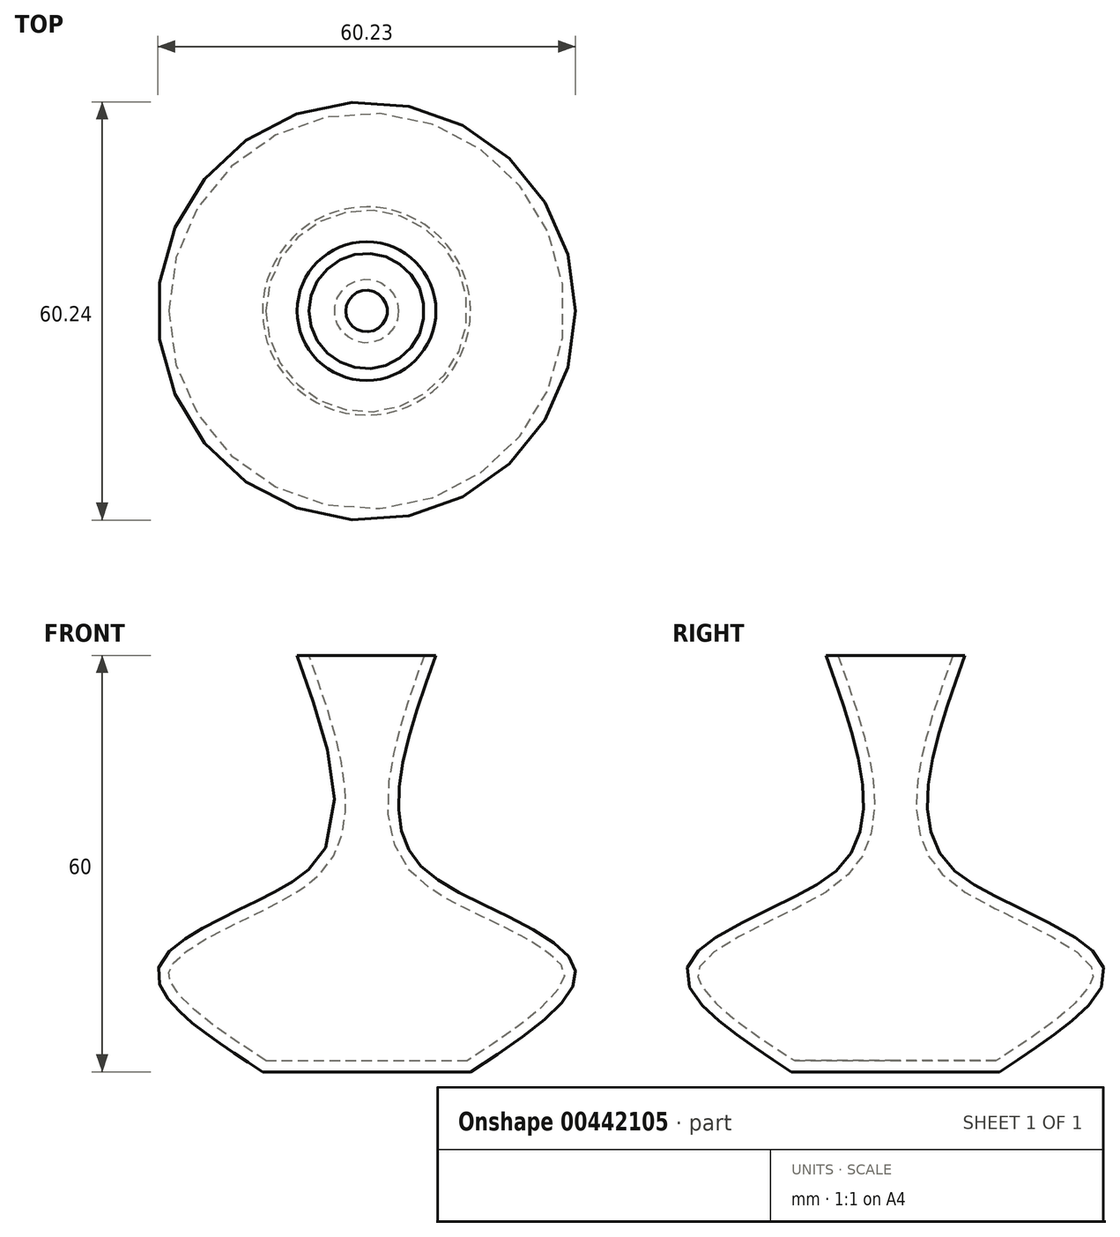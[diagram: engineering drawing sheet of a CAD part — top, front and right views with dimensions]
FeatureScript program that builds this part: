
annotation { "Feature Type Name" : "Feature", "Feature Type Description" : "" }
export const myFeature = defineFeature(function(context is Context, id is Id, definition is map)
    precondition{}
    {
        {
            var Q0;
            Q0=qCreatedBy(makeId("Top.planeOp"),FACE);
            var sketch = newSketch(context, id + "F0", { "sketchPlane" : qUnion([Q0])});
            skCircle(sketch, "E0", {"center": v(0, 0) * mm, "radius": 15 * mm});
            skSolve(sketch);
        }
        {
            var Q0;
            Q0=qCreatedBy(makeId("Top.planeOp"),FACE);
            cPlane(context, id + "F1", {"entities" : qUnion([Q0]), "cplaneType" : CPlaneType.OFFSET, "offset" : 15 * mm, "width" : 150 * mm, "height" : 150 * mm});
        }
        {
            var Q0;
            Q0=qCreatedBy(id+"F1.planeOp",FACE);
            var sketch = newSketch(context, id + "F2", { "sketchPlane" : qUnion([Q0])});
            skCircle(sketch, "E1", {"center": v(0, 0) * mm, "radius": 30 * mm});
            skSolve(sketch);
        }
        {
            var Q0;
            Q0=qCreatedBy(id+"F1.planeOp",FACE);
            cPlane(context, id + "F3", {"entities" : qUnion([Q0]), "cplaneType" : CPlaneType.OFFSET, "offset" : 10 * mm, "width" : 150 * mm, "height" : 150 * mm});
        }
        {
            var Q0;
            Q0=qCreatedBy(id+"F3.planeOp",FACE);
            var sketch = newSketch(context, id + "F4", { "sketchPlane" : qUnion([Q0])});
            skCircle(sketch, "E2", {"center": v(0, 0) * mm, "radius": 15 * mm});
            skSolve(sketch);
        }
        {
            var Q0;
            Q0=qCreatedBy(id+"F3.planeOp",FACE);
            cPlane(context, id + "F5", {"entities" : qUnion([Q0]), "cplaneType" : CPlaneType.OFFSET, "offset" : 5 * mm, "width" : 150 * mm, "height" : 150 * mm});
        }
        {
            var Q0;
            Q0=qCreatedBy(id+"F5.planeOp",FACE);
            var sketch = newSketch(context, id + "F6", { "sketchPlane" : qUnion([Q0])});
            skCircle(sketch, "E3", {"center": v(0, 0) * mm, "radius": 7.5 * mm});
            skSolve(sketch);
        }
        {
            var Q0;
            Q0=qCreatedBy(id+"F5.planeOp",FACE);
            cPlane(context, id + "F7", {"entities" : qUnion([Q0]), "cplaneType" : CPlaneType.OFFSET, "offset" : 30 * mm, "width" : 150 * mm, "height" : 150 * mm});
        }
        {
            var Q0;
            Q0=qCreatedBy(id+"F7.planeOp",FACE);
            var sketch = newSketch(context, id + "F8", { "sketchPlane" : qUnion([Q0])});
            skCircle(sketch, "E4", {"center": v(0, 0) * mm, "radius": 10 * mm});
            skSolve(sketch);
        }
        {
            var Q0;
            Q0=makeQuery(id+"F0.imprint","IMPRINT",FACE,{"disambiguationData":[TD([[makeQuery(id+"F0.imprint","IMPRINT",EDGE,{"derivedFrom":sQuery(id+"F0.wireOp",EDGE,"E0")}),1.0]])]});
            var Q1;
            Q1=makeQuery(id+"F2.imprint","IMPRINT",FACE,{"disambiguationData":[TD([[makeQuery(id+"F2.imprint","IMPRINT",EDGE,{"derivedFrom":sQuery(id+"F2.wireOp",EDGE,"E1")}),1.0]])]});
            var Q2;
            Q2=makeQuery(id+"F4.imprint","IMPRINT",FACE,{"disambiguationData":[TD([[makeQuery(id+"F4.imprint","IMPRINT",EDGE,{"derivedFrom":sQuery(id+"F4.wireOp",EDGE,"E2")}),1.0]])]});
            var Q3;
            Q3=makeQuery(id+"F6.imprint","IMPRINT",FACE,{"disambiguationData":[TD([[makeQuery(id+"F6.imprint","IMPRINT",EDGE,{"derivedFrom":sQuery(id+"F6.wireOp",EDGE,"E3")}),1.0]])]});
            var Q4;
            Q4=makeQuery(id+"F8.imprint","IMPRINT",FACE,{"disambiguationData":[TD([[makeQuery(id+"F8.imprint","IMPRINT",EDGE,{"derivedFrom":sQuery(id+"F8.wireOp",EDGE,"E4")}),1.0]])]});
            loft(context, id + "F9", {"sheetProfilesArray" : [{ "sheetProfileEntities" : qUnion([Q0]) }, { "sheetProfileEntities" : qUnion([Q1]) }, { "sheetProfileEntities" : qUnion([Q2]) }, { "sheetProfileEntities" : qUnion([Q3]) }, { "sheetProfileEntities" : qUnion([Q4]) }]});
        }
        {
            var Q0;
            Q0=makeQuery(id+"F9.opLoft","CAP_FACE",FACE,{"disambiguationData":[OSD([makeQuery(id+"F8.imprint","IMPRINT",FACE,{"disambiguationData":[TD([[makeQuery(id+"F8.imprint","IMPRINT",EDGE,{"derivedFrom":sQuery(id+"F8.wireOp",EDGE,"E4")}),1.0]])]})])],"isStart":true});
            shell(context, id + "F10", {"entities" : qUnion([Q0]), "thickness" : 1.6 * mm});
        }
    });
